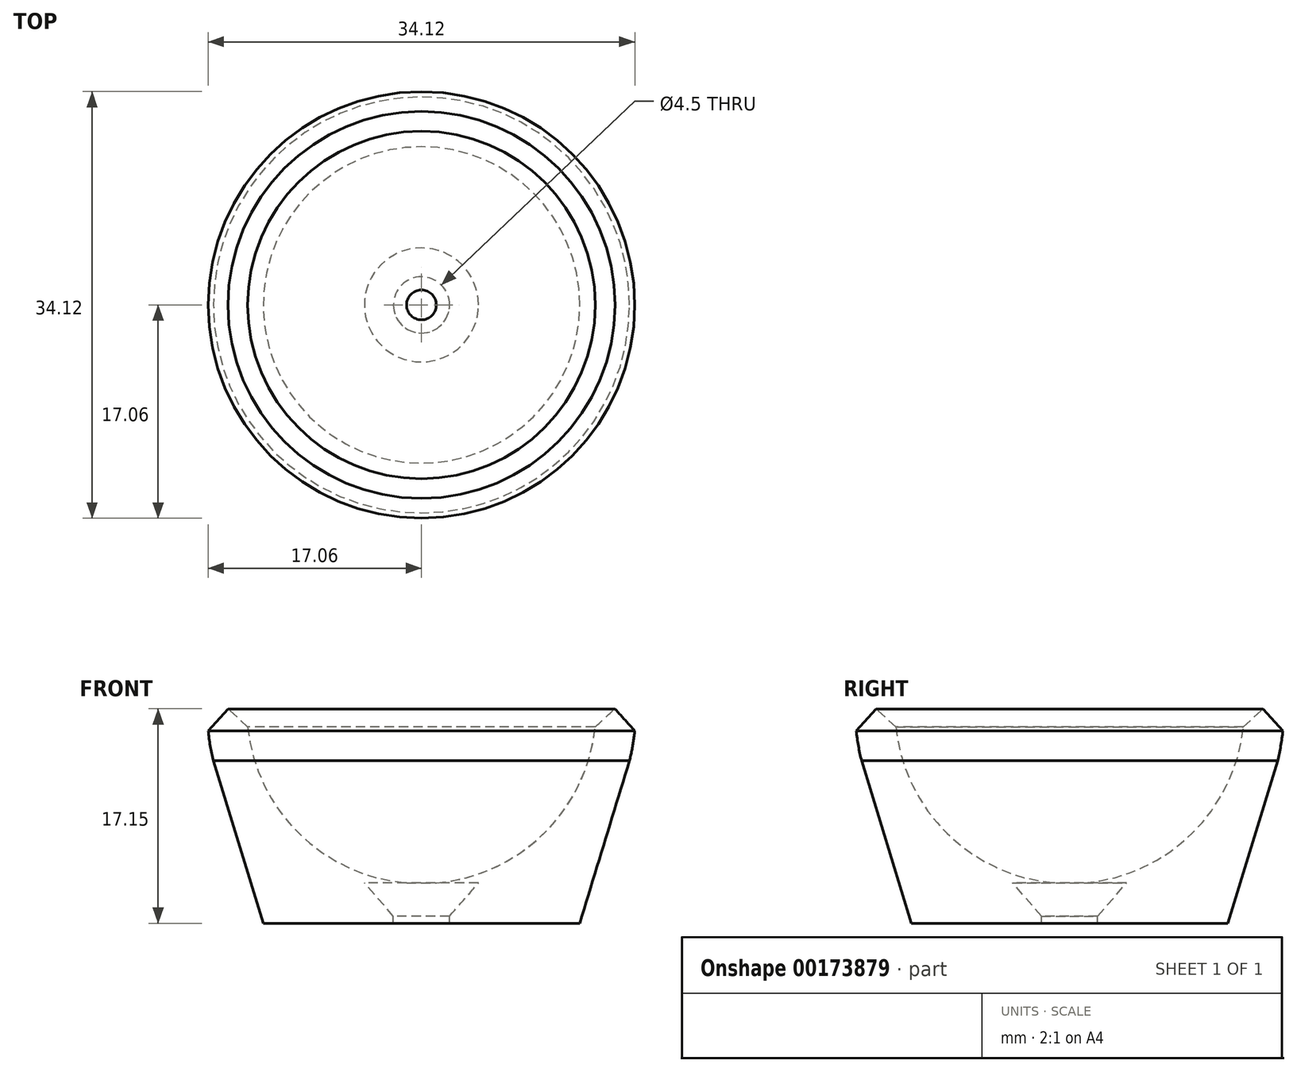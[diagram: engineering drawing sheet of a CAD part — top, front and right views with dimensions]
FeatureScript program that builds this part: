
annotation { "Feature Type Name" : "Feature", "Feature Type Description" : "" }
export const myFeature = defineFeature(function(context is Context, id is Id, definition is map)
    precondition{}
    {
        {
            var Q0;
            Q0=qCreatedBy(makeId("Right.planeOp"),FACE);
            var sketch = newSketch(context, id + "F0", { "sketchPlane" : qUnion([Q0])});
            skArc(sketch, "E0", {"start": v(-17.15, 17.14) * mm, "mid": v(-17.02, 15.05) * mm, "end": v(-16.63, 13) * mm});
            skArc(sketch, "E1", {"start": v(-13.97, 17.15) * mm, "mid": v(-9.88, 7.27) * mm, "end": v(0, 3.18) * mm});
            skLineSegment(sketch, "E2", {"start": v(-13.97, 17.14) * mm, "end": v(-17.14, 17.14) * mm});
            skLineSegment(sketch, "E3", {"start": v(0, 3.18) * mm, "end": v(0, 0) * mm});
            skLineSegment(sketch, "E4", {"start": v(-16.63, 13) * mm, "end": v(-12.65, 0) * mm});
            skLineSegment(sketch, "E5", {"start": v(-12.65, 0) * mm, "end": v(0, 0) * mm});
            skSolve(sketch);
        }
        {
            var Q0;
            Q0=makeQuery(id+"F0.imprint","IMPRINT",FACE,{"disambiguationData":[TD([[makeQuery(id+"F0.imprint","IMPRINT",EDGE,{"derivedFrom":sQuery(id+"F0.wireOp",EDGE,"AJDgylYy-vgsV-32Zp-rH1t-KisQUmxQgYa7")}),-1.0]])]});
            var Q1;
            Q1=makeQuery(id+"F0.imprint","IMPRINT",FACE,{"disambiguationData":[TD([[makeQuery(id+"F0.imprint","IMPRINT",EDGE,{"derivedFrom":sQuery(id+"F0.wireOp",EDGE,"E0")}),1.0]])]});
            var Q2;
            Q2=sQuery(id+"F0.wireOp",EDGE,"E3");
            revolve(context, id + "F1", {"entities" : qUnion([Q0, Q1]), "axis" : qUnion([Q2]), "revolveType" : RevolveType.FULL});
        }
        {
            var Q0;
            Q0=qCreatedBy(makeId("Top.planeOp"),FACE);
            cPlane(context, id + "F2", {"entities" : qUnion([Q0]), "cplaneType" : CPlaneType.OFFSET, "offset" : 3.23 * mm, "width" : 152.4 * mm, "height" : 152.4 * mm});
        }
        {
            var Q0;
            Q0=qCreatedBy(id+"F2.planeOp",FACE);
            var sketch = newSketch(context, id + "F3", { "sketchPlane" : qUnion([Q0])});
            skPoint(sketch, "E6", {"position": v(0, 0) * mm});
            skSolve(sketch);
        }
        {
            var Q0;
            Q0=makeQuery(id+"F1.opRevolve","SWEPT_EDGE",EDGE,{"disambiguationData":[OSD([sQuery(id+"F0.wireOp",EDGE,"E1"),sQuery(id+"F0.wireOp",EDGE,"E2")])]});
            var Q1;
            Q1=makeQuery(id+"F1.opRevolve","SWEPT_EDGE",EDGE,{"disambiguationData":[OSD([sQuery(id+"F0.wireOp",EDGE,"E0"),sQuery(id+"F0.wireOp",EDGE,"E2")])]});
            chamfer(context, id + "F4", {"entities" : qUnion([Q0, Q1]), "width" : 1.59 * mm, "tangentPropagation" : true});
        }
        {
            var Q0;
            Q0=sQuery(id+"F3.wireOp",VERTEX,"E6");
            var Q1;
            Q1=makeQuery(id+"F1.opRevolve","SWEPT_BODY",BODY,{"disambiguationData":[OSD([sQuery(id+"F0.wireOp",EDGE,"E0"),sQuery(id+"F0.wireOp",EDGE,"E1"),sQuery(id+"F0.wireOp",EDGE,"E2"),sQuery(id+"F0.wireOp",EDGE,"E3"),sQuery(id+"F0.wireOp",EDGE,"E4"),sQuery(id+"F0.wireOp",EDGE,"E5")])]});
            hole(context, id + "F5", {"style" : HoleStyle.C_SINK, "endStyle" : HoleEndStyle.BLIND, "standardTappedOrClearance" : lookupTablePath({ "standard" : "ANSI", "fit" : "Normal (ASME)", "size" : "#8", "type" : "Clearance" }), "standardBlindInLast" : lookupTablePath({ "fit" : "Free", "standard" : "ANSI", "size" : "#8", "type" : "Clearance" }), "holeDiameter" : 4.5 * mm, "cSinkDiameter" : 9.12 * mm, "cSinkAngle" : 82 * degree, "holeDepth" : 12.7 * mm, "locations" : qUnion([Q0]), "scope" : qUnion([Q1])});
        }
    });
